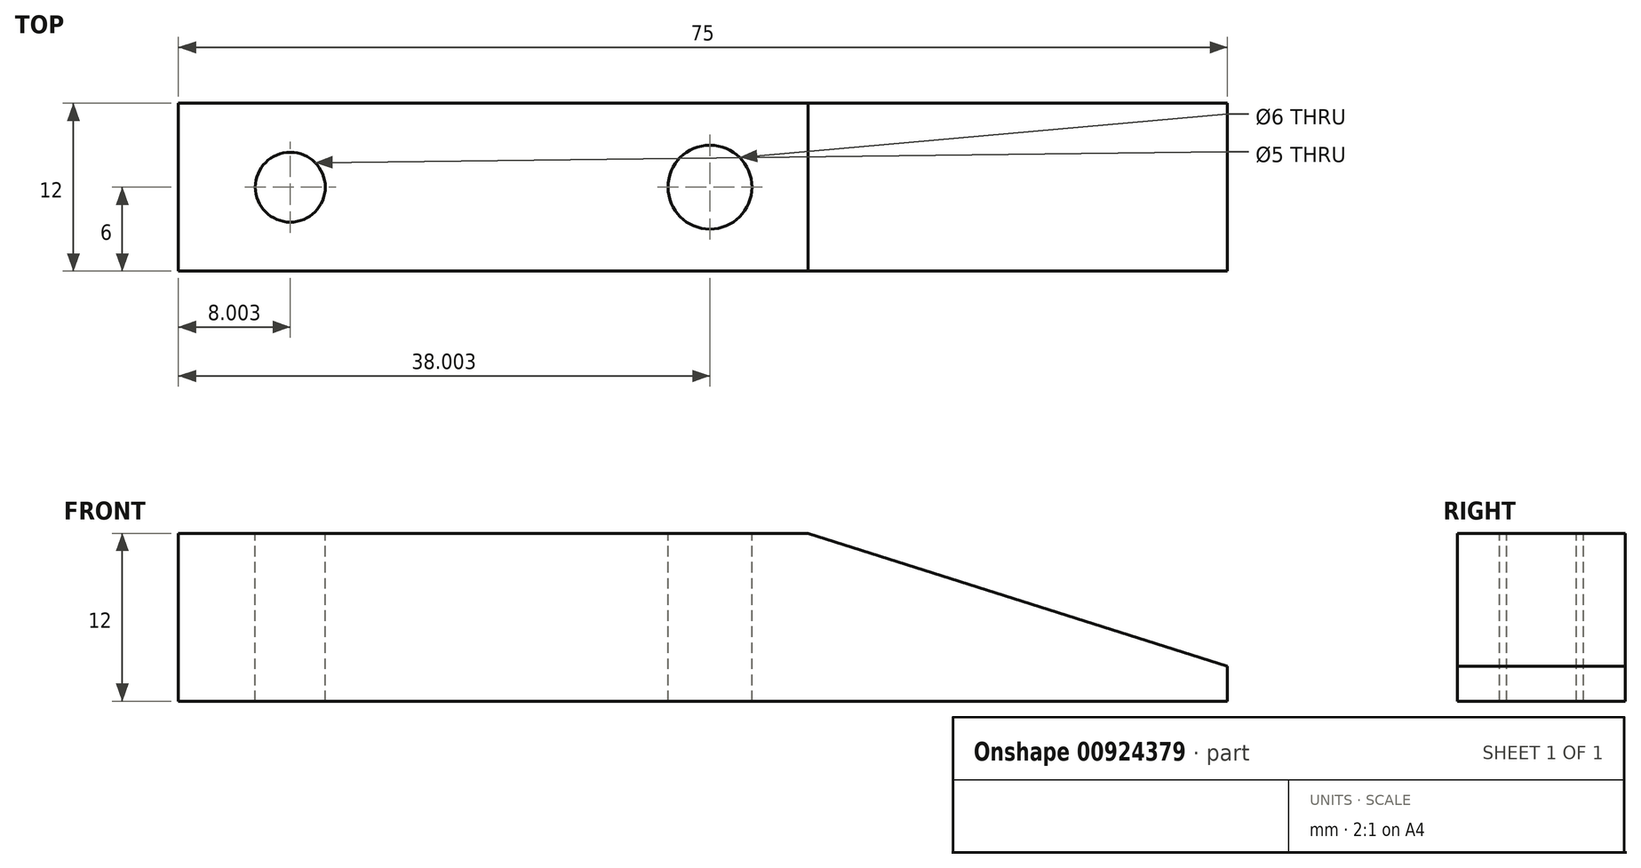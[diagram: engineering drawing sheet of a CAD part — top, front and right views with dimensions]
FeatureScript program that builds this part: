
annotation { "Feature Type Name" : "Feature", "Feature Type Description" : "" }
export const myFeature = defineFeature(function(context is Context, id is Id, definition is map)
    precondition{}
    {
        {
            var Q0;
            Q0=qCreatedBy(makeId("Front.planeOp"),FACE);
            var sketch = newSketch(context, id + "F0", { "sketchPlane" : qUnion([Q0])});
            skLineSegment(sketch, "E0", {"start": v(-51.72, 43.92) * mm, "end": v(-6.72, 43.92) * mm});
            skLineSegment(sketch, "E1", {"start": v(-6.72, 43.92) * mm, "end": v(23.28, 34.42) * mm});
            skLineSegment(sketch, "E2", {"start": v(23.28, 34.42) * mm, "end": v(23.28, 31.92) * mm});
            skLineSegment(sketch, "E3", {"start": v(23.28, 31.92) * mm, "end": v(-51.72, 31.92) * mm});
            skLineSegment(sketch, "E4", {"start": v(-51.72, 31.92) * mm, "end": v(-51.72, 43.92) * mm});
            skSolve(sketch);
        }
        {
            var Q0;
            Q0 = qSketchRegion(id + "F0", true);
            extrude(context, id + "F1", {"entities" : qUnion([Q0]), "depth" : 12 * mm, "offsetDistance" : 25 * mm});
        }
        {
            var Q0;
            Q0=makeQuery(id+"F1.opExtrude","SWEPT_FACE",FACE,{"disambiguationData":[OSD([sQuery(id+"F0.wireOp",EDGE,"E0")])]});
            var sketch = newSketch(context, id + "F2", { "sketchPlane" : qUnion([Q0])});
            skCircle(sketch, "E5", {"center": v(-43.72, -6) * mm, "radius": 2.5 * mm});
            skCircle(sketch, "E6", {"center": v(-13.72, -6) * mm, "radius": 3 * mm});
            skSolve(sketch);
        }
        {
            var Q0;
            Q0=makeQuery(id+"F2.imprint","IMPRINT",FACE,{"disambiguationData":[TD([[makeQuery(id+"F2.imprint","IMPRINT",EDGE,{"derivedFrom":sQuery(id+"F2.wireOp",EDGE,"E5")}),1.0]])]});
            var Q1;
            Q1=makeQuery(id+"F2.imprint","IMPRINT",FACE,{"disambiguationData":[TD([[makeQuery(id+"F2.imprint","IMPRINT",EDGE,{"derivedFrom":sQuery(id+"F2.wireOp",EDGE,"E6")}),1.0]])]});
            extrude(context, id + "F3", {"entities" : qUnion([Q0, Q1]), "operationType" : NewBodyOperationType.REMOVE, "oppositeDirection" : true, "depth" : 25 * mm, "offsetDistance" : 25 * mm});
        }
    });
